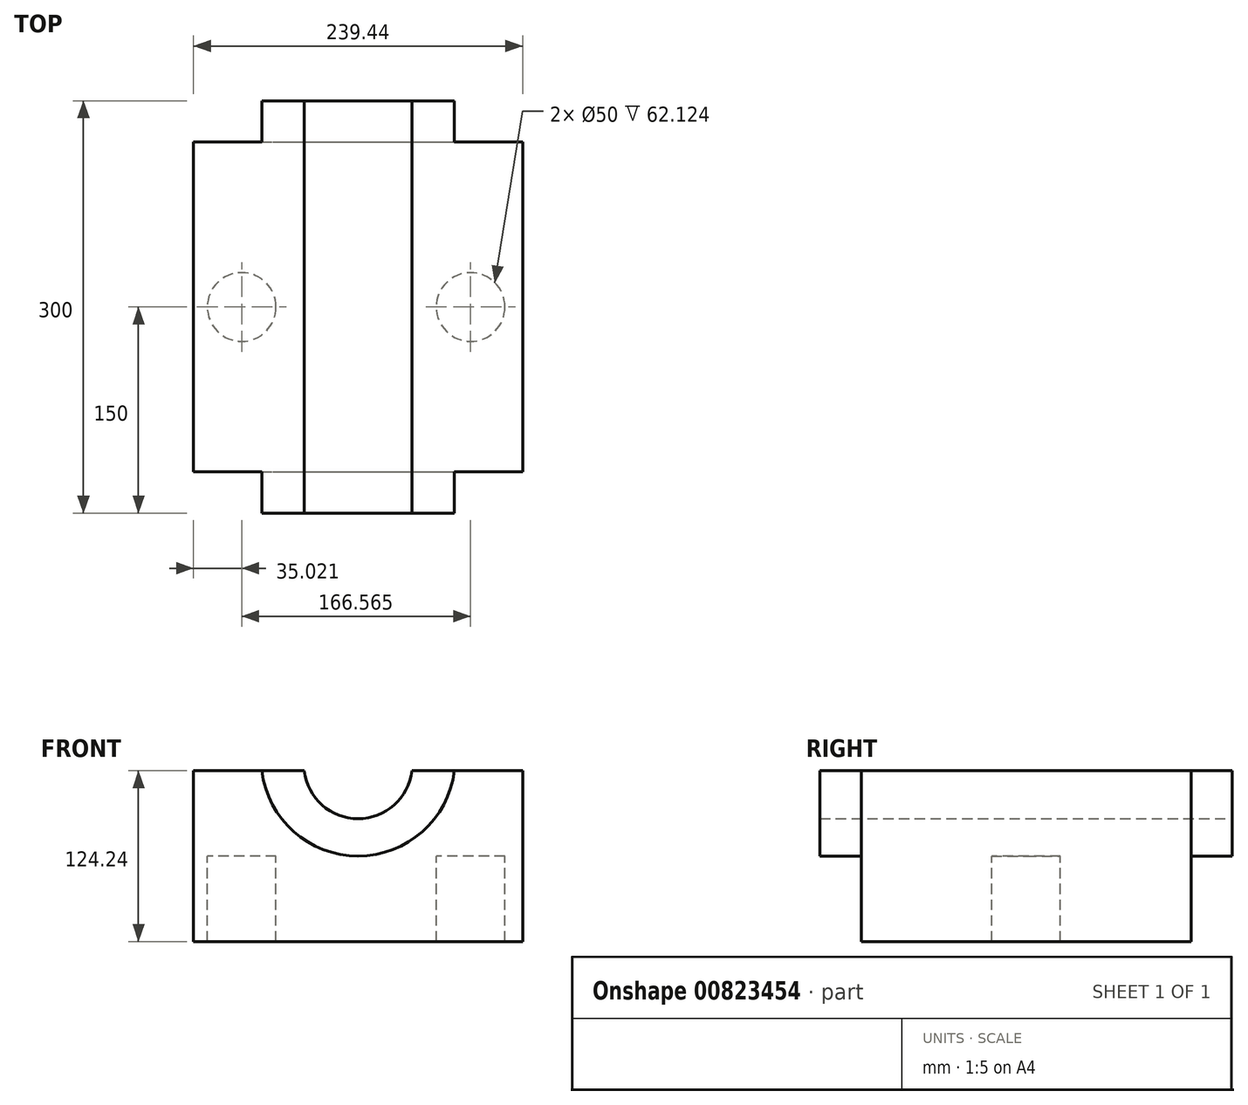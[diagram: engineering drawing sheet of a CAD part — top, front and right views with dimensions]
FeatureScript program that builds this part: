
annotation { "Feature Type Name" : "Feature", "Feature Type Description" : "" }
export const myFeature = defineFeature(function(context is Context, id is Id, definition is map)
    precondition{}
    {
        {
            var Q0;
            Q0=qCreatedBy(makeId("Front.planeOp"),FACE);
            var sketch = newSketch(context, id + "F0", { "sketchPlane" : qUnion([Q0])});
            skLineSegment(sketch, "E0.bottom", {"start": v(-119.72, 62.12) * mm, "end": v(119.72, 62.12) * mm});
            skLineSegment(sketch, "E0.top", {"start": v(-119.72, -62.12) * mm, "end": v(119.72, -62.12) * mm});
            skLineSegment(sketch, "E0.left", {"start": v(-119.72, 62.12) * mm, "end": v(-119.72, -62.12) * mm});
            skLineSegment(sketch, "E0.right", {"start": v(119.72, 62.12) * mm, "end": v(119.72, -62.12) * mm});
            skPoint(sketch, "E0.middle", {"position": v(0, 0) * mm});
            skLineSegment(sketch, "E1.bottom", {"start": v(-70.05, 62.12) * mm, "end": v(70.05, 62.12) * mm});
            skLineSegment(sketch, "E1.top", {"start": v(-70.05, -62.12) * mm, "end": v(70.05, -62.12) * mm});
            skLineSegment(sketch, "E1.left", {"start": v(-70.05, 62.12) * mm, "end": v(-70.05, -62.12) * mm});
            skLineSegment(sketch, "E1.right", {"start": v(70.05, 62.12) * mm, "end": v(70.05, -62.12) * mm});
            skArc(sketch, "E2", {"start": v(-70.05, 62.12) * mm, "mid": v(0, 0.1) * mm, "end": v(70.05, 62.12) * mm});
            skLineSegment(sketch, "E3.bottom", {"start": v(-39.2, 62.12) * mm, "end": v(39.2, 62.12) * mm});
            skLineSegment(sketch, "E3.top", {"start": v(-39.2, 26.87) * mm, "end": v(39.2, 26.87) * mm});
            skLineSegment(sketch, "E3.left", {"start": v(-39.2, 62.12) * mm, "end": v(-39.2, 26.87) * mm});
            skLineSegment(sketch, "E3.right", {"start": v(39.2, 62.12) * mm, "end": v(39.2, 26.87) * mm});
            skPoint(sketch, "E3.middle", {"position": v(0, 44.5) * mm});
            skArc(sketch, "E4", {"start": v(-39.2, 62.12) * mm, "mid": v(0, 27.27) * mm, "end": v(39.2, 62.12) * mm});
            skSolve(sketch);
        }
        {
            var Q0;
            {var subQ0=sQuery(id+"F0.wireOp",EDGE,"E2");Q0=makeQuery(id+"F0.imprint","IMPRINT",FACE,{"disambiguationData":[TD([[makeQuery(id+"F0.imprint","IMPRINT",EDGE,{"derivedFrom":subQ0}),1.0]])]});}
            var Q1;
            Q1=makeQuery(id+"F0.imprint","IMPRINT",FACE,{"disambiguationData":[TD([[makeQuery(id+"F0.imprint","IMPRINT",EDGE,{"derivedFrom":sQuery(id+"F0.wireOp",EDGE,"E3.top")}),1.0]])]});
            extrude(context, id + "F1", {"entities" : qUnion([Q0, Q1]), "depth" : 150 * mm, "offsetDistance" : 25 * mm, "hasSecondDirection" : true, "secondDirectionOppositeDirection" : true, "secondDirectionDepth" : 150 * mm});
        }
        {
            var Q0;
            {var subQ0=sQuery(id+"F0.wireOp",EDGE,"E0.left");Q0=makeQuery(id+"F0.imprint","IMPRINT",FACE,{"disambiguationData":[TD([[makeQuery(id+"F0.imprint","IMPRINT",EDGE,{"derivedFrom":subQ0}),1.0]])]});}
            var Q1;
            {var subQ0=sQuery(id+"F0.wireOp",EDGE,"E1.left");Q1=makeQuery(id+"F0.imprint","IMPRINT",FACE,{"disambiguationData":[TD([[makeQuery(id+"F0.imprint","IMPRINT",EDGE,{"derivedFrom":subQ0}),1.0]])]});}
            var Q2;
            {var subQ0=sQuery(id+"F0.wireOp",EDGE,"E0.right");Q2=makeQuery(id+"F0.imprint","IMPRINT",FACE,{"disambiguationData":[TD([[makeQuery(id+"F0.imprint","IMPRINT",EDGE,{"derivedFrom":subQ0}),-1.0]])]});}
            extrude(context, id + "F2", {"entities" : qUnion([Q0, Q1, Q2]), "operationType" : NewBodyOperationType.ADD, "depth" : 120 * mm, "offsetDistance" : 25 * mm, "hasSecondDirection" : true, "secondDirectionOppositeDirection" : true, "secondDirectionDepth" : 120 * mm});
        }
        {
            var Q0;
            Q0=qCreatedBy(makeId("Top.planeOp"),FACE);
            var sketch = newSketch(context, id + "F3", { "sketchPlane" : qUnion([Q0])});
            skCircle(sketch, "E5", {"center": v(-84.7, 0) * mm, "radius": 30.3 * mm});
            skCircle(sketch, "E6", {"center": v(81.87, 0) * mm, "radius": 31.05 * mm});
            skSolve(sketch);
        }
        {
            var Q0;
            Q0=sQuery(id+"F3.wireOp",VERTEX,"E5.center");
            var Q1;
            Q1=sQuery(id+"F3.wireOp",VERTEX,"E6.center");
            var Q2;
            Q2=makeQuery(id+"F1.opExtrude","SWEPT_BODY",BODY,{"disambiguationData":[OSD([sQuery(id+"F0.wireOp",EDGE,"E0.bottom"),sQuery(id+"F0.wireOp",EDGE,"E2"),sQuery(id+"F0.wireOp",EDGE,"E4")])]});
            hole(context, id + "F4", {"style" : HoleStyle.SIMPLE, "endStyle" : HoleEndStyle.THROUGH, "holeDiameter" : 50 * mm, "majorDiameter" : 5 * mm, "isTappedThrough" : true, "tappedDepth" : 12 * mm, "tapClearance" : 3, "locations" : qUnion([Q0, Q1]), "scope" : qUnion([Q2])});
        }
    });
